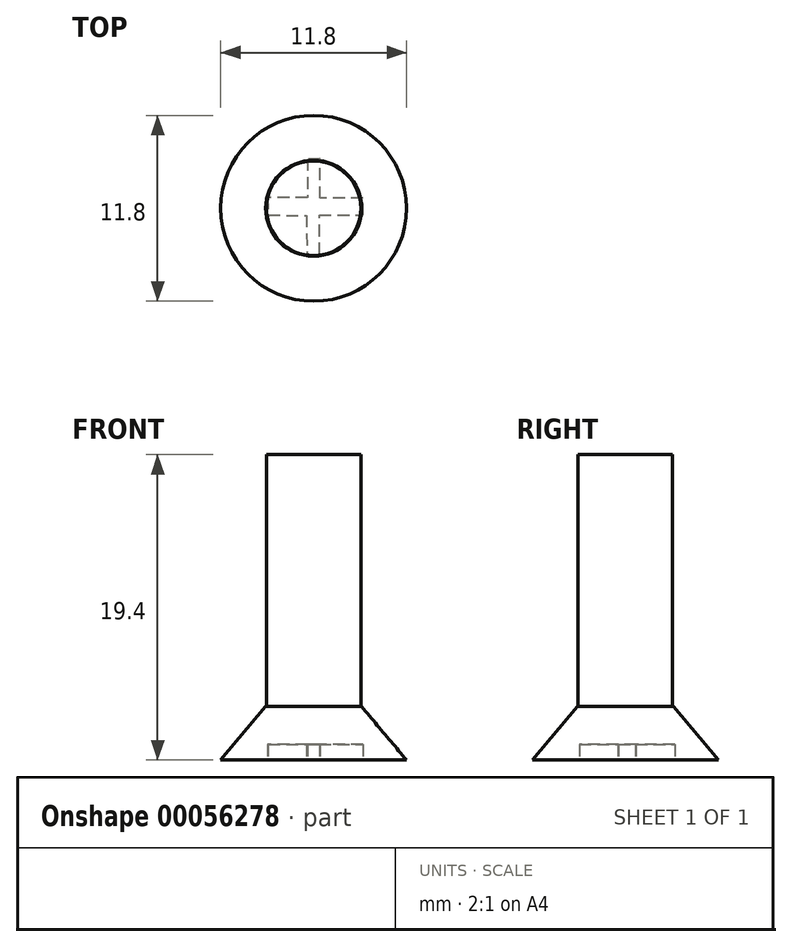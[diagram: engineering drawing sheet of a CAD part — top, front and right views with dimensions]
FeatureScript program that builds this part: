
annotation { "Feature Type Name" : "Feature", "Feature Type Description" : "" }
export const myFeature = defineFeature(function(context is Context, id is Id, definition is map)
    precondition{}
    {
        {
            var Q0;
            Q0=qCreatedBy(makeId("Top.planeOp"),FACE);
            var sketch = newSketch(context, id + "F0", { "sketchPlane" : qUnion([Q0])});
            skCircle(sketch, "E0", {"center": v(0, 0) * mm, "radius": 5.9 * mm});
            skSolve(sketch);
        }
        {
            var Q0;
            Q0=qSketchRegion(id+"F0",true);
            extrude(context, id + "F1", {"entities" : qUnion([Q0]), "depth" : 3.4 * mm, "hasDraft" : true, "draftAngle" : 40 * degree, "draftPullDirection" : true});
        }
        {
            var Q0;
            Q0=makeQuery(id+"F1.opExtrude","CAP_FACE",FACE,{"disambiguationData":[OSD([sQuery(id+"F0.wireOp",EDGE,"E0")])],"isStart":false});
            var sketch = newSketch(context, id + "F2", { "sketchPlane" : qUnion([Q0])});
            skCircle(sketch, "E1", {"center": v(0, 0) * mm, "radius": 3 * mm});
            skSolve(sketch);
        }
        {
            var Q0;
            Q0=qSketchRegion(id+"F2",true);
            extrude(context, id + "F3", {"entities" : qUnion([Q0]), "operationType" : NewBodyOperationType.ADD, "depth" : 16 * mm});
        }
        {
            var Q0;
            Q0=makeQuery(id+"F1.opExtrude","CAP_FACE",FACE,{"disambiguationData":[OSD([sQuery(id+"F0.wireOp",EDGE,"E0")])],"isStart":true});
            var sketch = newSketch(context, id + "F4", { "sketchPlane" : qUnion([Q0])});
            skLineSegment(sketch, "E2", {"start": v(-0.41, 2.93) * mm, "end": v(0.37, 2.93) * mm});
            skLineSegment(sketch, "E3", {"start": v(0.37, 2.93) * mm, "end": v(0.37, 0.44) * mm});
            skLineSegment(sketch, "E4", {"start": v(0.37, 0.44) * mm, "end": v(3.13, 0.44) * mm});
            skLineSegment(sketch, "E5", {"start": v(3.13, 0.44) * mm, "end": v(3.13, -0.64) * mm});
            skLineSegment(sketch, "E6", {"start": v(3.13, -0.64) * mm, "end": v(0.41, -0.64) * mm});
            skLineSegment(sketch, "E7", {"start": v(0.41, -0.64) * mm, "end": v(0.41, -3.16) * mm});
            skLineSegment(sketch, "E8", {"start": v(0.41, -3.16) * mm, "end": v(-0.4, -3.13) * mm});
            skLineSegment(sketch, "E9", {"start": v(-0.4, -3.13) * mm, "end": v(-0.4, -0.69) * mm});
            skLineSegment(sketch, "E10", {"start": v(-0.4, -0.69) * mm, "end": v(-2.93, -0.69) * mm});
            skLineSegment(sketch, "E11", {"start": v(-2.93, -0.69) * mm, "end": v(-2.88, 0.44) * mm});
            skLineSegment(sketch, "E12", {"start": v(-2.88, 0.44) * mm, "end": v(-0.46, 0.46) * mm});
            skLineSegment(sketch, "E13", {"start": v(-0.46, 0.46) * mm, "end": v(-0.41, 2.93) * mm});
            skSolve(sketch);
        }
        {
            var Q0;
            Q0=qSketchRegion(id+"F4",true);
            extrude(context, id + "F5", {"entities" : qUnion([Q0]), "operationType" : NewBodyOperationType.REMOVE, "oppositeDirection" : true, "depth" : 1 * mm});
        }
    });
